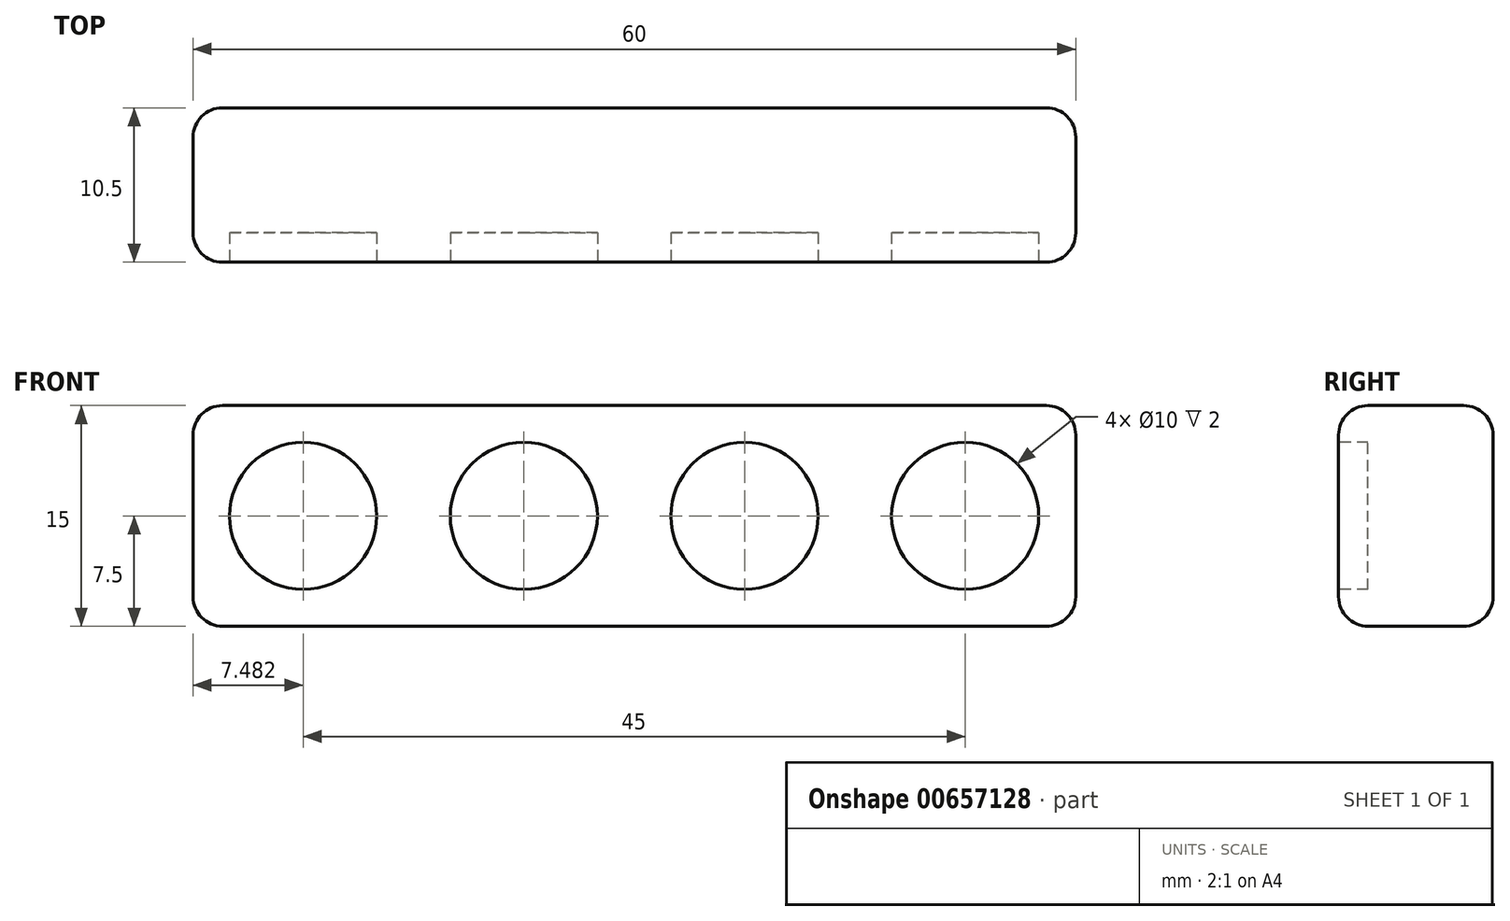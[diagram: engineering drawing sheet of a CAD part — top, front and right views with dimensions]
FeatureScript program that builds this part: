
annotation { "Feature Type Name" : "Feature", "Feature Type Description" : "" }
export const myFeature = defineFeature(function(context is Context, id is Id, definition is map)
    precondition{}
    {
        {
            var Q0;
            Q0=qCreatedBy(makeId("Front.planeOp"),FACE);
            var sketch = newSketch(context, id + "F0", { "sketchPlane" : qUnion([Q0])});
            skLineSegment(sketch, "E0.bottom", {"start": v(30, -7.5) * mm, "end": v(-30, -7.5) * mm});
            skLineSegment(sketch, "E0.top", {"start": v(30, 7.5) * mm, "end": v(-30, 7.5) * mm});
            skLineSegment(sketch, "E0.left", {"start": v(30, -7.5) * mm, "end": v(30, 7.5) * mm});
            skLineSegment(sketch, "E0.right", {"start": v(-30, -7.5) * mm, "end": v(-30, 7.5) * mm});
            skPoint(sketch, "E0.middle", {"position": v(0, 0) * mm});
            skSolve(sketch);
        }
        {
            var Q0;
            Q0=makeQuery(id+"F0.imprint","IMPRINT",FACE,{"disambiguationData":[TD([[makeQuery(id+"F0.imprint","IMPRINT",EDGE,{"derivedFrom":sQuery(id+"F0.wireOp",EDGE,"E0.bottom")}),-1.0]])]});
            extrude(context, id + "F1", {"entities" : qUnion([Q0]), "depth" : 10.5 * mm, "offsetDistance" : 25 * mm});
        }
        {
            var Q0;
            Q0=makeQuery(id+"F1.opExtrude","CAP_FACE",FACE,{"disambiguationData":[OSD([sQuery(id+"F0.wireOp",EDGE,"E0.bottom"),sQuery(id+"F0.wireOp",EDGE,"E0.top"),sQuery(id+"F0.wireOp",EDGE,"E0.left"),sQuery(id+"F0.wireOp",EDGE,"E0.right")])],"isStart":false});
            var sketch = newSketch(context, id + "F2", { "sketchPlane" : qUnion([Q0])});
            skCircle(sketch, "E1", {"center": v(-22.52, 0) * mm, "radius": 5 * mm});
            skCircle(sketch, "E2.1.0.0", {"center": v(-7.52, 0) * mm, "radius": 5 * mm});
            skLineSegment(sketch, "E2.direction1", {"start": v(-22.52, 0) * mm, "end": v(-7.52, 0) * mm, "construction": true});
            skCircle(sketch, "E3.0.2.0", {"center": v(7.48, 0) * mm, "radius": 5 * mm});
            skCircle(sketch, "E3.0.3.0", {"center": v(22.48, 0) * mm, "radius": 5 * mm});
            skPoint(sketch, "E4", {"position": v(-30, 0) * mm});
            skSolve(sketch);
        }
        {
            var Q0;
            Q0=makeQuery(id+"F2.imprint","IMPRINT",FACE,{"disambiguationData":[TD([[makeQuery(id+"F2.imprint","IMPRINT",EDGE,{"derivedFrom":sQuery(id+"F2.wireOp",EDGE,"E1")}),1.0]])]});
            var Q1;
            Q1=makeQuery(id+"F2.imprint","IMPRINT",FACE,{"disambiguationData":[TD([[makeQuery(id+"F2.imprint","IMPRINT",EDGE,{"derivedFrom":sQuery(id+"F2.wireOp",EDGE,"E2.1.0.0")}),1.0]])]});
            var Q2;
            Q2=makeQuery(id+"F2.imprint","IMPRINT",FACE,{"disambiguationData":[TD([[makeQuery(id+"F2.imprint","IMPRINT",EDGE,{"derivedFrom":sQuery(id+"F2.wireOp",EDGE,"f0d1a3c5-8c7a-4bfd-956c-8d08d1cac1ae0.MirrorC")}),-1.0]])]});
            var Q3;
            Q3=makeQuery(id+"F2.imprint","IMPRINT",FACE,{"disambiguationData":[TD([[makeQuery(id+"F2.imprint","IMPRINT",EDGE,{"derivedFrom":sQuery(id+"F2.wireOp",EDGE,"f0d1a3c5-8c7a-4bfd-956c-8d08d1cac1ae1.MirrorC")}),-1.0]])]});
            var Q4;
            Q4=makeQuery(id+"F2.imprint","IMPRINT",FACE,{"disambiguationData":[TD([[makeQuery(id+"F2.imprint","IMPRINT",EDGE,{"derivedFrom":sQuery(id+"F2.wireOp",EDGE,"E3.0.2.0")}),1.0]])]});
            var Q5;
            Q5=makeQuery(id+"F2.imprint","IMPRINT",FACE,{"disambiguationData":[TD([[makeQuery(id+"F2.imprint","IMPRINT",EDGE,{"derivedFrom":sQuery(id+"F2.wireOp",EDGE,"E3.0.3.0")}),1.0]])]});
            extrude(context, id + "F3", {"entities" : qUnion([Q0, Q1, Q2, Q3, Q4, Q5]), "operationType" : NewBodyOperationType.REMOVE, "oppositeDirection" : true, "depth" : 2 * mm, "offsetDistance" : 25 * mm});
        }
        {
            var Q0;
            Q0=makeQuery(id+"F1.opExtrude","SWEPT_EDGE",EDGE,{"disambiguationData":[OSD([sQuery(id+"F0.wireOp",EDGE,"E0.top"),sQuery(id+"F0.wireOp",EDGE,"E0.right")])]});
            var Q1;
            Q1=makeQuery(id+"F1.opExtrude","CAP_EDGE",EDGE,{"disambiguationData":[OSD([sQuery(id+"F0.wireOp",EDGE,"E0.left")])],"isStart":true});
            var Q2;
            Q2=makeQuery(id+"F1.opExtrude","CAP_EDGE",EDGE,{"disambiguationData":[OSD([sQuery(id+"F0.wireOp",EDGE,"E0.top")])],"isStart":false});
            var Q3;
            Q3=makeQuery(id+"F1.opExtrude","CAP_EDGE",EDGE,{"disambiguationData":[OSD([sQuery(id+"F0.wireOp",EDGE,"E0.top")])],"isStart":true});
            var Q4;
            Q4=makeQuery(id+"F1.opExtrude","SWEPT_EDGE",EDGE,{"disambiguationData":[OSD([sQuery(id+"F0.wireOp",EDGE,"E0.top"),sQuery(id+"F0.wireOp",EDGE,"E0.left")])]});
            var Q5;
            Q5=makeQuery(id+"F1.opExtrude","SWEPT_EDGE",EDGE,{"disambiguationData":[OSD([sQuery(id+"F0.wireOp",EDGE,"E0.bottom"),sQuery(id+"F0.wireOp",EDGE,"E0.left")])]});
            var Q6;
            Q6=makeQuery(id+"F1.opExtrude","CAP_EDGE",EDGE,{"disambiguationData":[OSD([sQuery(id+"F0.wireOp",EDGE,"E0.left")])],"isStart":false});
            var Q7;
            Q7=makeQuery(id+"F1.opExtrude","CAP_EDGE",EDGE,{"disambiguationData":[OSD([sQuery(id+"F0.wireOp",EDGE,"E0.bottom")])],"isStart":true});
            var Q8;
            Q8=makeQuery(id+"F1.opExtrude","CAP_EDGE",EDGE,{"disambiguationData":[OSD([sQuery(id+"F0.wireOp",EDGE,"E0.right")])],"isStart":true});
            var Q9;
            Q9=makeQuery(id+"F1.opExtrude","SWEPT_EDGE",EDGE,{"disambiguationData":[OSD([sQuery(id+"F0.wireOp",EDGE,"E0.bottom"),sQuery(id+"F0.wireOp",EDGE,"E0.right")])]});
            var Q10;
            Q10=makeQuery(id+"F1.opExtrude","CAP_EDGE",EDGE,{"disambiguationData":[OSD([sQuery(id+"F0.wireOp",EDGE,"E0.right")])],"isStart":false});
            var Q11;
            Q11=makeQuery(id+"F1.opExtrude","CAP_EDGE",EDGE,{"disambiguationData":[OSD([sQuery(id+"F0.wireOp",EDGE,"E0.bottom")])],"isStart":false});
            fillet(context, id + "F4", {"entities" : qUnion([Q0, Q1, Q2, Q3, Q4, Q5, Q6, Q7, Q8, Q9, Q10, Q11]), "radius" : 2 * mm, "tangentPropagation" : true, "allowEdgeOverflow" : false});
        }
    });
